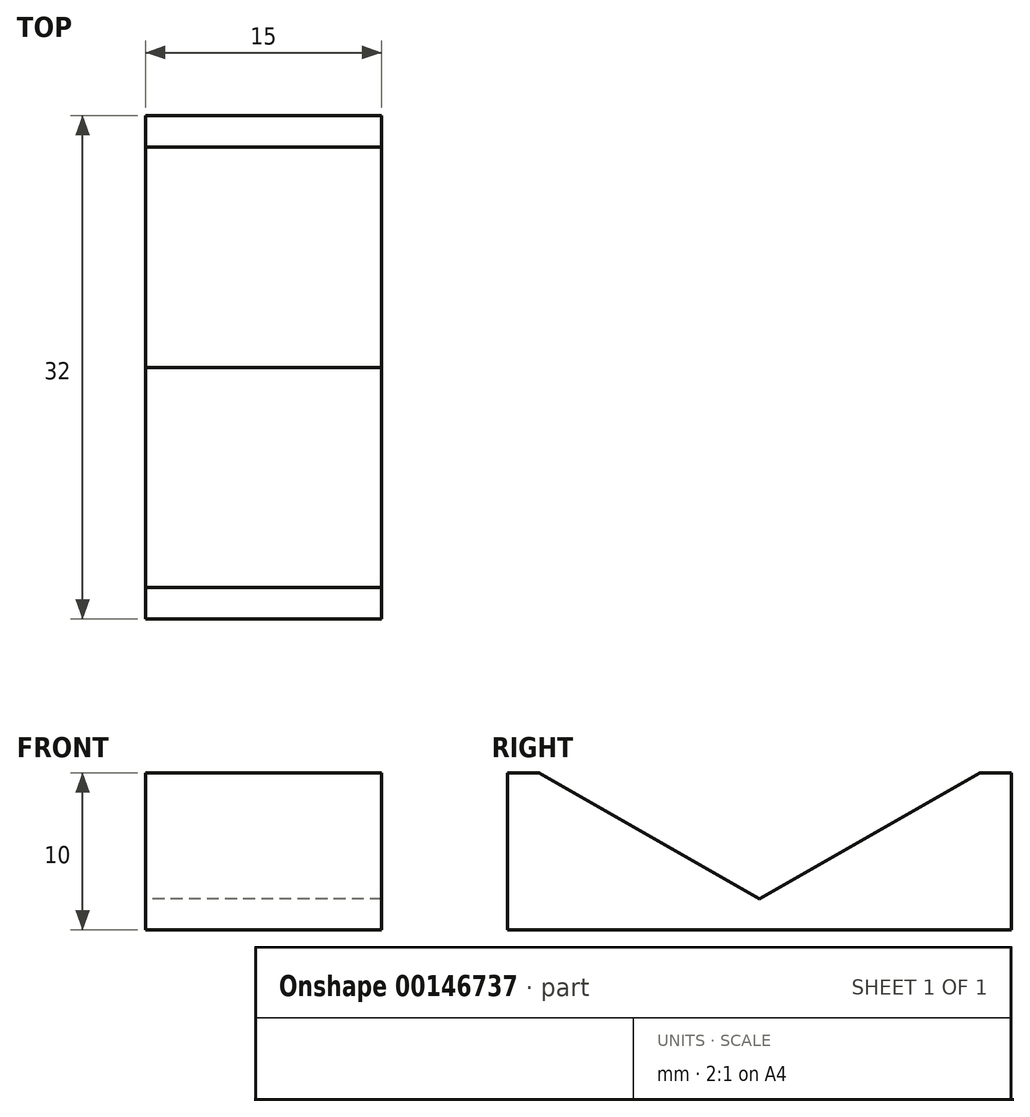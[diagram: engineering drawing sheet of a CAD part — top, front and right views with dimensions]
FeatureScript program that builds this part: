
annotation { "Feature Type Name" : "Feature", "Feature Type Description" : "" }
export const myFeature = defineFeature(function(context is Context, id is Id, definition is map)
    precondition{}
    {
        {
            var Q0;
            Q0=qCreatedBy(makeId("Right.planeOp"),FACE);
            var sketch = newSketch(context, id + "F0", { "sketchPlane" : qUnion([Q0])});
            skLineSegment(sketch, "E0", {"start": v(0, 0) * mm, "end": v(16, 0) * mm});
            skLineSegment(sketch, "E1", {"start": v(16, 0) * mm, "end": v(16, 10) * mm});
            skLineSegment(sketch, "E2", {"start": v(16, 10) * mm, "end": v(14, 10) * mm});
            skLineSegment(sketch, "E3", {"start": v(14, 10) * mm, "end": v(0, 2) * mm});
            skLineSegment(sketch, "E4", {"start": v(0, 2) * mm, "end": v(0, 0) * mm});
            skSolve(sketch);
        }
        {
            var Q0;
            Q0=makeQuery(id+"F0.imprint","IMPRINT",FACE,{"disambiguationData":[TD([[makeQuery(id+"F0.imprint","IMPRINT",EDGE,{"derivedFrom":sQuery(id+"F0.wireOp",EDGE,"E0")}),1.0]])]});
            extrude(context, id + "F1", {"entities" : qUnion([Q0]), "depth" : 15 * mm});
        }
        {
            var Q0;
            Q0=makeQuery(id+"F1.opExtrude","SWEPT_BODY",BODY,{"disambiguationData":[OSD([sQuery(id+"F0.wireOp",EDGE,"E0"),sQuery(id+"F0.wireOp",EDGE,"E1"),sQuery(id+"F0.wireOp",EDGE,"E2"),sQuery(id+"F0.wireOp",EDGE,"E3"),sQuery(id+"F0.wireOp",EDGE,"E4")])]});
            var Q1;
            Q1=makeQuery(id+"F1.opExtrude","SWEPT_FACE",FACE,{"disambiguationData":[OSD([sQuery(id+"F0.wireOp",EDGE,"E4")])]});
            mirror(context, id + "F2", {"operationType" : NewBodyOperationType.ADD, "entities" : qUnion([Q0]), "mirrorPlane" : qUnion([Q1])});
        }
    });
